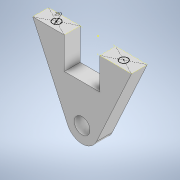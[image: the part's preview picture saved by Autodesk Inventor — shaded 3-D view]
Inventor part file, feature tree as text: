
AUTODESK INVENTOR PART (.ipt)
format: ipt  version: 2020 (Build 240168000, 168)  size: 119,808 bytes
history: native  units: in
note: dims shown in document units (in); Inventor stores cm internally (conversion verified against a paired STEP export)
features: sketch x2, extrude x1
ambient origin geometry x8: Origin, YZ Plane, XZ Plane, XY Plane, X Axis, Y Axis, Z Axis, Center Point
bodies: Solid1 (feature_tree)
feature tree (3):
  extrude  "Extrusion1"  Depth=0.5in
  sketch  "Sketch2"  dims[d2=1.125in d3=0.25in d4=1.0in d6=1.0in d7=0.5in d8=0.0in d9=0.25in]
  sketch  "Sketch1"  dims[d0=0.5in d1=2.205in]
